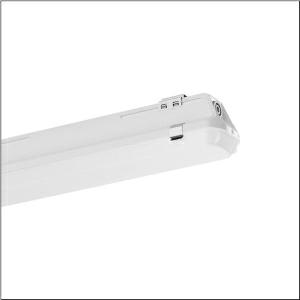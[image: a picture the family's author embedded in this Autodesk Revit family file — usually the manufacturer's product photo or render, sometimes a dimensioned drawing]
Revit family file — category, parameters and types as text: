
# Revit family: monsun_r__21_chemical_51fb30mp480b_6f39
name_source: partatom
category: Lighting Fixtures
units: mm (PartAtom-declared; Revit-internal decimal feet)

## family parameters
Cut with Voids When Loaded = No
Host = Face
Light Source = No
Part Type = Normal
Room Calculation Point = No
Round Connector Dimension = Use Diameter
Shared = No

## types (1)
- --- (1 x LED, 7750 lm, 53.6 W, 4000K)
    Apparent Load = 54 VA
    CIE Flux Codes = 48 77 93 95 100
    Color Rendering = 80
    Color Temperature = 4000K
    Default Elevation = 1800 mm
    Description = Monsun® 21 chemical, damp-proof luminaire, chain hanger, primary optical cover: enclosure, of PA, light emission: direct distribution, primary light characteristic: symmetric, installation type: suspended mounting, surface-mounted, horizontal mounting, vertical mounting, LED, rated luminous flux: 7.750lm, luminous efficacy: 145lm/W, light colour: 840, colour temperature: 4000K, control gear: ECG, with terminal, 3-pole, max. 2.5mm², mains connection: 220..240V, AC, 50/60Hz, rated input power: 54W, housing, of glass-fibre reinforced polyester, uncoated, bright grey, incl. chain hanger, length: 1.590mm, width: 90mm, height: 88mm, clip for enclosure, of stainless steel (V2A), ceiling mounting element, of stainless steel (V2A), chain hanger, of stainless steel (V2A), protection rating (complete): IP66, insulation class (complete): insulation class I (protective earthing), certification: CE, ENEC, VDE, UKCA, protection symbol: D, impact resistance: IK08, permissible operating ambient temperature: -25..+35°C, standard: EN 50419, EN 60598-2-1, corresponds to IFS (International Featured Standards) requirements for safety and quality in the food industry, for indoor or canopied outdoor use, no direct snow, no direct sun, no direct rain, contact your sales advisor before using the luminaires in applications with unclear chemical exposure, large temperature fluctuations or condensation-forming humidity, LABS conformity tested according to VDMA 24364:2018-05, packaging unit: 1 piece
    Height = 89 mm
    Lamp = 1 x LED
    Lamp Light Flux = 7750 lm
    Lamp Power = 53.6 W
    Lamp count = 1
    Length = 1590 mm
    Luminous efficacy = 145 lm/W
    Manufacturer = Siteco
    ModVariant = No
    Model = 51FB30MP480B
    Mounting Place = Ceiling
    Mounting Type = Surface mounted
    Number of Poles = 1
    OnlyDefault = Yes
    Power Factor = 1
    Product Name = Monsun® 21 chemical
    Product group = damp-proof luminaire
    ProductGroupID = 300
    Protection Class = Protection class I
    Protection Degree = IP 66
    RLX_Detail_Level = 1
    RLX_Emergency_Light_Flux = 0 lm
    RLX_Emergency_Type = 0
    RLX_Emergency_Type_DB = No
    RlxData = <blob elided: 89753 chars, md5=8b8eaafc>
    Socket = socket
    Standby Power = 0 W
    System Light Flux = 7750 lm
    System Power = 54 W
    Type Comments = factory setting: luminous flux: 100 % | (A | C | E) | 121 mA
    Type Image = l_1006717.jpg
    URL = http://relux.com
    VarID = @adj_079277
    Voltage = 0 V
    Weight = 0.00 kg
    Width = 90 mm

## geometry (parser evidence)
native form markers: Blend x4, Sweep x12
no freeform markers — native parametric forms only
